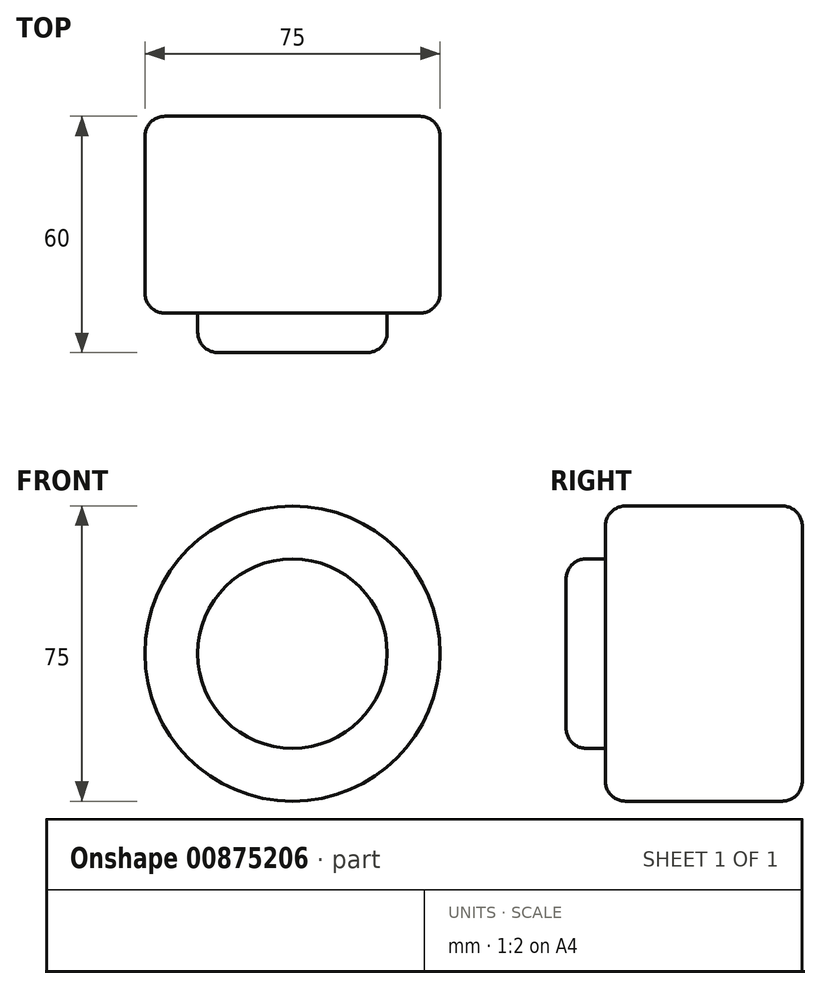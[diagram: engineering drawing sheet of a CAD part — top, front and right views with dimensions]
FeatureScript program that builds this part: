
annotation { "Feature Type Name" : "Feature", "Feature Type Description" : "" }
export const myFeature = defineFeature(function(context is Context, id is Id, definition is map)
    precondition{}
    {
        {
            var Q0;
            Q0=qCreatedBy(makeId("Front.planeOp"),FACE);
            var sketch = newSketch(context, id + "F0", { "sketchPlane" : qUnion([Q0])});
            skCircle(sketch, "E0", {"center": v(0, 0) * mm, "radius": 37.5 * mm});
            skSolve(sketch);
        }
        {
            var Q0;
            Q0=makeQuery(id+"F0.imprint","IMPRINT",FACE,{"disambiguationData":[TD([[makeQuery(id+"F0.imprint","IMPRINT",EDGE,{"derivedFrom":sQuery(id+"F0.wireOp",EDGE,"E0")}),1.0]])]});
            extrude(context, id + "F1", {"entities" : qUnion([Q0]), "depth" : 50 * mm, "offsetDistance" : 25.4 * mm});
        }
        {
            var Q0;
            Q0=makeQuery(id+"F1.opExtrude","CAP_FACE",FACE,{"disambiguationData":[OSD([sQuery(id+"F0.wireOp",EDGE,"E0")])],"isStart":false});
            var sketch = newSketch(context, id + "F2", { "sketchPlane" : qUnion([Q0])});
            skCircle(sketch, "E1", {"center": v(0, 0) * mm, "radius": 24.07 * mm});
            skSolve(sketch);
        }
        {
            var Q0;
            Q0 = qSketchRegion(id + "F2", true);
            extrude(context, id + "F3", {"entities" : qUnion([Q0]), "operationType" : NewBodyOperationType.ADD, "depth" : 10 * mm, "offsetDistance" : 25.4 * mm});
        }
        {
            var Q0;
            Q0=makeQuery(id+"F1.opExtrude","SWEPT_FACE",FACE,{"disambiguationData":[OSD([sQuery(id+"F0.wireOp",EDGE,"E0")])]});
            fillet(context, id + "F4", {"entities" : qUnion([Q0]), "radius" : 5.08 * mm, "tangentPropagation" : true, "allowEdgeOverflow" : false});
        }
        {
            var Q0;
            Q0=makeQuery(id+"F3.opExtrude","CAP_FACE",FACE,{"disambiguationData":[OSD([sQuery(id+"F2.wireOp",EDGE,"E1")])],"isStart":false});
            fillet(context, id + "F5", {"entities" : qUnion([Q0]), "radius" : 5.08 * mm, "tangentPropagation" : true, "allowEdgeOverflow" : false});
        }
    });
